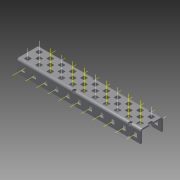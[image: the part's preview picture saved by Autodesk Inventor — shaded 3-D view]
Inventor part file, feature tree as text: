
AUTODESK INVENTOR PART (.ipt)
format: ipt  version: 2015 (Build 190159000, 159)  size: 2,023,936 bytes
history: native  units: in
note: dims shown in document units (in); Inventor stores cm internally (conversion verified against a paired STEP export)
features: other x61, pattern_linear x3, sheet_metal_op x1, extrude x1, imported_body x1, sketch x1
ambient origin geometry x8: Origin, YZ Plane, XZ Plane, XY Plane, X Axis, Y Axis, Z Axis, Center Point
bodies: Body1 (feature_tree)
feature tree (68):
  sheet_metal_op  "Fold1"
  other  "C-Channel"
  extrude  "length cut"  Depth=0.5in
  other  "top axis"
  other  "inner axis"
  other  "front axis"
  other  "back axis"
  pattern_linear  "top axes"  Spacing1=0.5in  [1 undecoded]
  pattern_linear  "inner axes"  Spacing1=0.5in  [1 undecoded]
  pattern_linear  "horiz axes"  Spacing1=-5.5in  [1 undecoded]
  other  "right plane"
  imported_body  "Base1"
  sketch  "Sketch1"  dims[d1=0.0in d4=0.5in d5=0.7874in d7=0.5in d10=0.5in d13=0.5in d14=-5.5in d15=0.0in d16=0.0in d17=0.0in d18=0.0in d19=0.0in]
  other  "Work Point1"
  other  "Work Point2"
  other  "Work Point3"
  other  "Work Point4"
  other  "Work Axis5"
  other  "Work Axis6"
  other  "Work Axis7"
  other  "Work Axis8"
  other  "Work Axis11"
  other  "Work Axis12"
  other  "Work Axis13"
  other  "Work Axis14"
  other  "Work Axis15"
  other  "Work Axis18"
  other  "Work Axis19"
  other  "Work Axis20"
  other  "Work Axis23"
  other  "Work Axis24"
  other  "Work Axis25"
  other  "Work Axis26"
  other  "Work Axis30"
  other  "Work Axis31"
  other  "Work Axis32"
  other  "Work Axis33"
  other  "left plane"
  other  "Work Axis37"
  other  "Work Axis38"
  other  "Work Axis39"
  other  "Work Axis40"
  other  "Work Axis41"
  other  "Work Axis42"
  other  "Work Axis57"
  other  "Work Axis58"
  other  "Work Axis59"
  other  "Work Axis60"
  other  "Work Axis61"
  other  "Work Axis62"
  other  "Work Axis77"
  other  "Work Axis78"
  other  "Work Axis79"
  other  "Work Axis80"
  other  "Work Axis81"
  other  "Work Axis82"
  other  "Work Axis97"
  other  "Work Axis98"
  other  "Work Axis99"
  other  "Work Axis100"
  other  "Work Axis101"
  other  "Work Axis102"
  other  "Work Axis117"
  other  "Work Axis118"
  other  "Work Axis119"
  other  "Work Axis120"
  other  "Work Axis121"
  other  "Work Axis122"
note: 3 required parameter values undecoded (feature->parameter linkage not recoverable at this tier; creation-order binding heuristic only, values carry confidence <= 0.55)
